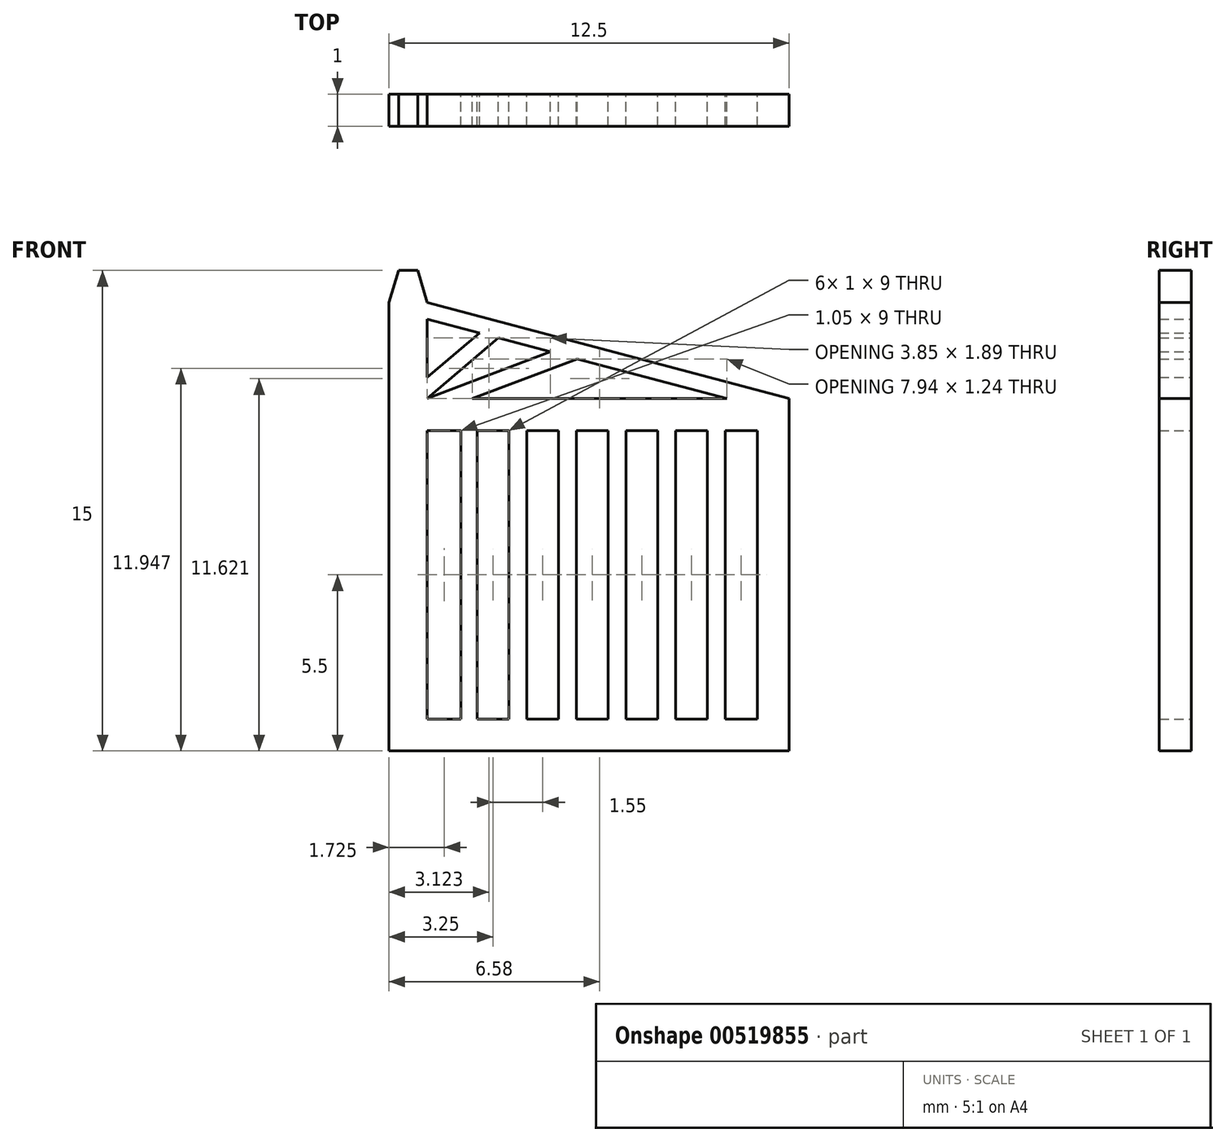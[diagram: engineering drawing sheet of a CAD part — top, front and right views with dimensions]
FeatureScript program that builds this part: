
annotation { "Feature Type Name" : "Feature", "Feature Type Description" : "" }
export const myFeature = defineFeature(function(context is Context, id is Id, definition is map)
    precondition{}
    {
        {
            var Q0;
            Q0=qCreatedBy(makeId("Front.planeOp"),FACE);
            var sketch = newSketch(context, id + "F0", { "sketchPlane" : qUnion([Q0])});
            skLineSegment(sketch, "E0", {"start": v(0, 0) * mm, "end": v(0, 14) * mm});
            skLineSegment(sketch, "E1", {"start": v(0, 14) * mm, "end": v(0.3, 15) * mm});
            skLineSegment(sketch, "E2", {"start": v(0.3, 15) * mm, "end": v(0.9, 15) * mm});
            skLineSegment(sketch, "E3", {"start": v(0.9, 15) * mm, "end": v(1.2, 14) * mm});
            skLineSegment(sketch, "E4", {"start": v(1.2, 14) * mm, "end": v(12.5, 11) * mm});
            skLineSegment(sketch, "E5", {"start": v(12.5, 11) * mm, "end": v(12.5, 0) * mm});
            skLineSegment(sketch, "E6", {"start": v(1.2, 13.48) * mm, "end": v(1.2, 11.66) * mm});
            skLineSegment(sketch, "E7", {"start": v(10.55, 11) * mm, "end": v(2.6, 11) * mm});
            skLineSegment(sketch, "E8", {"start": v(1.2, 10) * mm, "end": v(2.25, 10) * mm});
            skLineSegment(sketch, "E9", {"start": v(11.5, 10) * mm, "end": v(11.5, 1) * mm});
            skLineSegment(sketch, "E10", {"start": v(11.5, 1) * mm, "end": v(10.5, 1) * mm});
            skLineSegment(sketch, "E11", {"start": v(1.2, 13.48) * mm, "end": v(2.83, 13.05) * mm});
            skLineSegment(sketch, "E12.trimOffspring", {"start": v(1.2, 10) * mm, "end": v(1.2, 1) * mm});
            skLineSegment(sketch, "E13", {"start": v(2.6, 11) * mm, "end": v(5.88, 12.24) * mm});
            skLineSegment(sketch, "E14", {"start": v(1.2, 11) * mm, "end": v(3.41, 12.9) * mm});
            skLineSegment(sketch, "E15", {"start": v(1.2, 11.66) * mm, "end": v(2.83, 13.05) * mm});
            skLineSegment(sketch, "E16", {"start": v(1.2, 11) * mm, "end": v(5.05, 12.46) * mm});
            skLineSegment(sketch, "E17.trimOffspring", {"start": v(5.88, 12.24) * mm, "end": v(10.55, 11) * mm});
            skLineSegment(sketch, "E18.trimOffspring", {"start": v(3.41, 12.9) * mm, "end": v(5.05, 12.46) * mm});
            skLineSegment(sketch, "E19", {"start": v(12.5, 0) * mm, "end": v(0, 0) * mm});
            skLineSegment(sketch, "E20", {"start": v(10.5, 10) * mm, "end": v(10.5, 1) * mm});
            skLineSegment(sketch, "E21", {"start": v(9.95, 10) * mm, "end": v(9.95, 1) * mm});
            skLineSegment(sketch, "E22", {"start": v(8.95, 10) * mm, "end": v(8.95, 1) * mm});
            skLineSegment(sketch, "E23", {"start": v(8.4, 10) * mm, "end": v(8.4, 1) * mm});
            skLineSegment(sketch, "E24", {"start": v(7.4, 10) * mm, "end": v(7.4, 1) * mm});
            skLineSegment(sketch, "E25", {"start": v(6.85, 10) * mm, "end": v(6.85, 1) * mm});
            skLineSegment(sketch, "E26", {"start": v(5.85, 10) * mm, "end": v(5.85, 1) * mm});
            skLineSegment(sketch, "E27", {"start": v(5.3, 10) * mm, "end": v(5.3, 1) * mm});
            skLineSegment(sketch, "E28", {"start": v(4.3, 10) * mm, "end": v(4.3, 1) * mm});
            skLineSegment(sketch, "E29", {"start": v(3.75, 10) * mm, "end": v(3.75, 1) * mm});
            skLineSegment(sketch, "E30", {"start": v(2.75, 10) * mm, "end": v(2.75, 1) * mm});
            skLineSegment(sketch, "E31", {"start": v(2.25, 10) * mm, "end": v(2.25, 1) * mm});
            skLineSegment(sketch, "E32.trimOffspring", {"start": v(2.25, 1) * mm, "end": v(1.2, 1) * mm});
            skLineSegment(sketch, "E33.trimOffspring", {"start": v(3.75, 1) * mm, "end": v(2.75, 1) * mm});
            skLineSegment(sketch, "E34.trimOffspring", {"start": v(5.3, 1) * mm, "end": v(4.3, 1) * mm});
            skLineSegment(sketch, "E35.trimOffspring", {"start": v(6.85, 1) * mm, "end": v(5.85, 1) * mm});
            skLineSegment(sketch, "E36.trimOffspring", {"start": v(8.4, 1) * mm, "end": v(7.4, 1) * mm});
            skLineSegment(sketch, "E37.trimOffspring", {"start": v(9.95, 1) * mm, "end": v(8.95, 1) * mm});
            skLineSegment(sketch, "E38.trimOffspring", {"start": v(2.75, 10) * mm, "end": v(3.75, 10) * mm});
            skLineSegment(sketch, "E39.trimOffspring", {"start": v(4.3, 10) * mm, "end": v(5.3, 10) * mm});
            skLineSegment(sketch, "E40.trimOffspring", {"start": v(5.85, 10) * mm, "end": v(6.85, 10) * mm});
            skLineSegment(sketch, "E41.trimOffspring", {"start": v(7.4, 10) * mm, "end": v(8.4, 10) * mm});
            skLineSegment(sketch, "E42.trimOffspring", {"start": v(8.95, 10) * mm, "end": v(9.95, 10) * mm});
            skLineSegment(sketch, "E43.trimOffspring", {"start": v(10.5, 10) * mm, "end": v(11.5, 10) * mm});
            skSolve(sketch);
        }
        {
            var Q0;
            Q0 = qSketchRegion(id + "F0", true);
            extrude(context, id + "F1", {"entities" : qUnion([Q0]), "depth" : 1 * mm, "offsetDistance" : 25 * mm});
        }
    });
